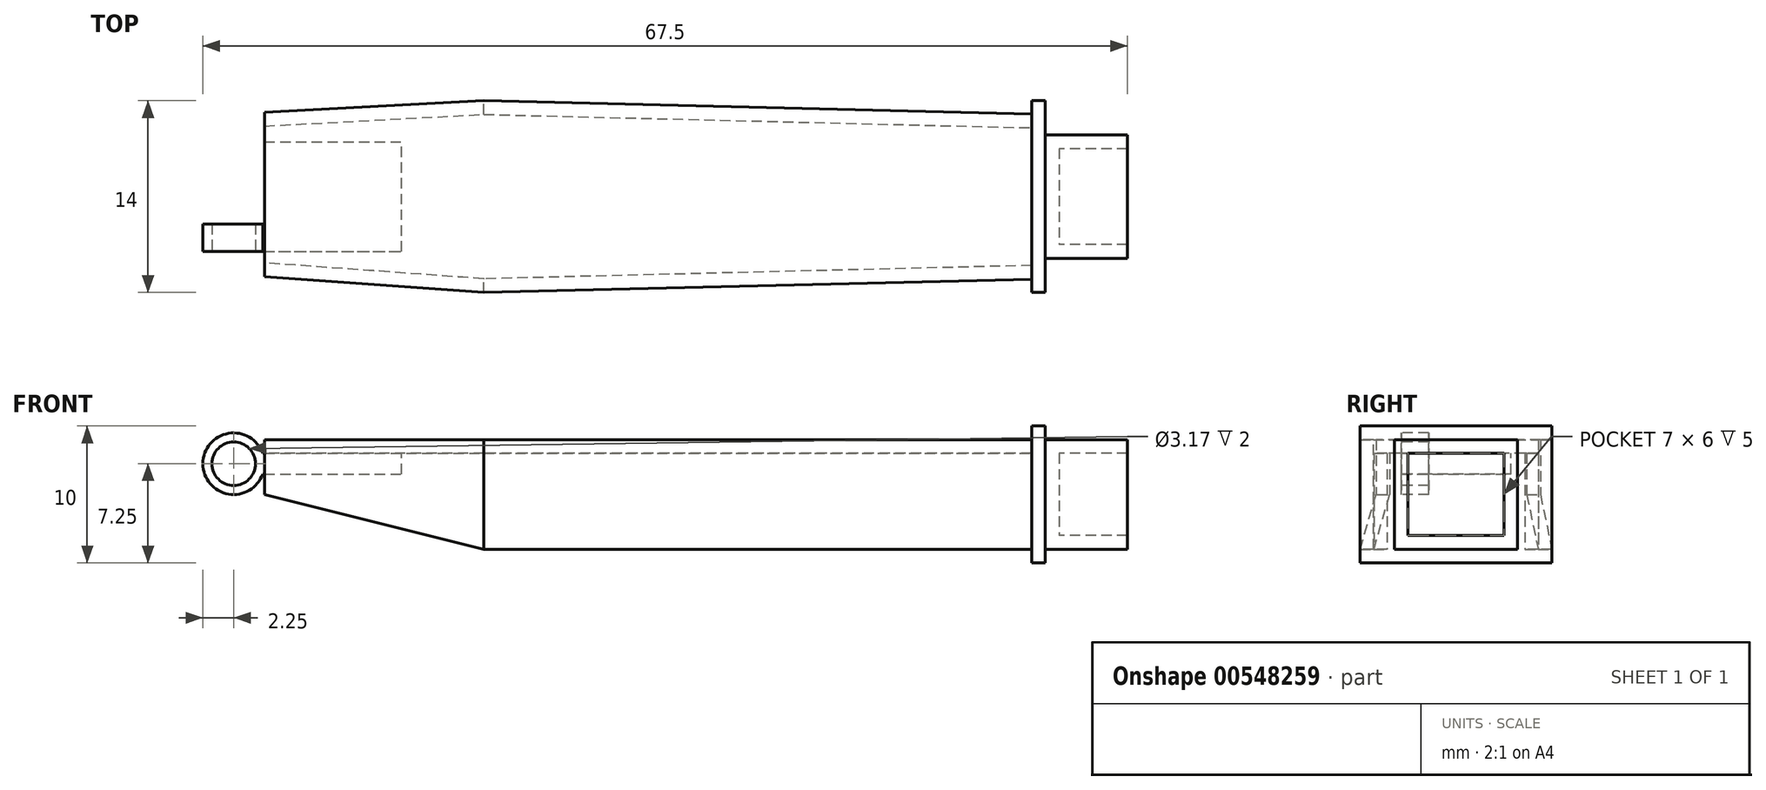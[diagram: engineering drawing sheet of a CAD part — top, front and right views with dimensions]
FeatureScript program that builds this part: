
annotation { "Feature Type Name" : "Feature", "Feature Type Description" : "" }
export const myFeature = defineFeature(function(context is Context, id is Id, definition is map)
    precondition{}
    {
        {
            var Q0;
            Q0=qCreatedBy(makeId("Top.planeOp"),FACE);
            var sketch = newSketch(context, id + "F0", { "sketchPlane" : qUnion([Q0])});
            skLineSegment(sketch, "E0", {"start": v(0, 6.16) * mm, "end": v(0, -5.84) * mm});
            skLineSegment(sketch, "E1", {"start": v(0, 6.16) * mm, "end": v(16, 7) * mm});
            skLineSegment(sketch, "E2", {"start": v(16, 7) * mm, "end": v(57, 6) * mm});
            skLineSegment(sketch, "E3", {"start": v(57, 6) * mm, "end": v(57, -6) * mm});
            skLineSegment(sketch, "E4", {"start": v(57, -6) * mm, "end": v(16, -7) * mm});
            skLineSegment(sketch, "E5", {"start": v(16, -7) * mm, "end": v(0, -5.84) * mm});
            skLineSegment(sketch, "E6", {"start": v(0, 0) * mm, "end": v(16, 0) * mm, "construction": true});
            skLineSegment(sketch, "E7", {"start": v(16, 7) * mm, "end": v(16, -7) * mm, "construction": true});
            skLineSegment(sketch, "E8", {"start": v(16, 0) * mm, "end": v(57, 0) * mm, "construction": true});
            skSolve(sketch);
        }
        {
            var Q0;
            Q0 = qSketchRegion(id + "F0", true);
            extrude(context, id + "F1", {"entities" : qUnion([Q0]), "depth" : 8 * mm, "offsetDistance" : 25 * mm});
        }
        {
            var Q0;
            Q0=makeQuery(id+"F1.opExtrude","CAP_FACE",FACE,{"disambiguationData":[OSD([sQuery(id+"F0.wireOp",EDGE,"E0"),sQuery(id+"F0.wireOp",EDGE,"E1"),sQuery(id+"F0.wireOp",EDGE,"E2"),sQuery(id+"F0.wireOp",EDGE,"E3"),sQuery(id+"F0.wireOp",EDGE,"E4"),sQuery(id+"F0.wireOp",EDGE,"E5")])],"isStart":true});
            var Q1;
            Q1=makeQuery(id+"F1.opExtrude","SWEPT_FACE",FACE,{"disambiguationData":[OSD([sQuery(id+"F0.wireOp",EDGE,"E0")])]});
            shell(context, id + "F2", {"entities" : qUnion([Q0, Q1]), "thickness" : 1 * mm});
        }
        {
            var Q0;
            Q0=qCreatedBy(makeId("Front.planeOp"),FACE);
            var sketch = newSketch(context, id + "F3", { "sketchPlane" : qUnion([Q0])});
            skLineSegment(sketch, "E9", {"start": v(0, 0) * mm, "end": v(0, 4) * mm});
            skLineSegment(sketch, "E10", {"start": v(0, 4) * mm, "end": v(16, 0) * mm});
            skLineSegment(sketch, "E11", {"start": v(16, 0) * mm, "end": v(0, 0) * mm});
            skLineSegment(sketch, "E12.0", {"start": v(57, 0) * mm, "end": v(16, 0) * mm, "construction": true});
            skSolve(sketch);
        }
        {
            var Q0;
            Q0 = qSketchRegion(id + "F3", true);
            extrude(context, id + "F4", {"entities" : qUnion([Q0]), "operationType" : NewBodyOperationType.REMOVE, "endBound" : BoundingType.SYMMETRIC, "depth" : 14.2 * mm, "offsetDistance" : 25 * mm});
        }
        {
            var Q0;
            Q0=makeQuery(id+"F1.opExtrude","SWEPT_FACE",FACE,{"disambiguationData":[OSD([sQuery(id+"F0.wireOp",EDGE,"E3")])]});
            var sketch = newSketch(context, id + "F5", { "sketchPlane" : qUnion([Q0])});
            skLineSegment(sketch, "E13.bottom", {"start": v(7, 9) * mm, "end": v(-7, 9) * mm});
            skLineSegment(sketch, "E13.top", {"start": v(7, -1) * mm, "end": v(-7, -1) * mm});
            skLineSegment(sketch, "E13.left", {"start": v(7, 9) * mm, "end": v(7, -1) * mm});
            skLineSegment(sketch, "E13.right", {"start": v(-7, 9) * mm, "end": v(-7, -1) * mm});
            skPoint(sketch, "E13.middle", {"position": v(0, 4) * mm});
            skPoint(sketch, "E13.middle.positionSnap0", {"position": v(6, 4) * mm});
            skPoint(sketch, "E13.centerSnap0", {"position": v(6, 4) * mm});
            skSolve(sketch);
        }
        {
            var Q0;
            Q0 = qSketchRegion(id + "F5", true);
            extrude(context, id + "F6", {"entities" : qUnion([Q0]), "operationType" : NewBodyOperationType.ADD, "oppositeDirection" : true, "depth" : 1 * mm, "offsetDistance" : 25 * mm});
        }
        {
            var Q0;
            Q0=makeQuery(id+"F6.boolean.opBoolean","MERGE",FACE,{"derivedFrom":[makeQuery(id+"F1.opExtrude","SWEPT_FACE",FACE,{"disambiguationData":[OSD([sQuery(id+"F0.wireOp",EDGE,"E3")])]}),makeQuery(id+"F6.opExtrude","CAP_FACE",FACE,{"disambiguationData":[OSD([sQuery(id+"F5.wireOp",EDGE,"E13.bottom"),sQuery(id+"F5.wireOp",EDGE,"E13.top"),sQuery(id+"F5.wireOp",EDGE,"E13.left"),sQuery(id+"F5.wireOp",EDGE,"E13.right")])],"isStart":true})]});
            var sketch = newSketch(context, id + "F7", { "sketchPlane" : qUnion([Q0])});
            skLineSegment(sketch, "E14.bottom", {"start": v(4.5, 8) * mm, "end": v(-4.5, 8) * mm});
            skLineSegment(sketch, "E14.top", {"start": v(4.5, 0) * mm, "end": v(-4.5, 0) * mm});
            skLineSegment(sketch, "E14.left", {"start": v(4.5, 8) * mm, "end": v(4.5, 0) * mm});
            skLineSegment(sketch, "E14.right", {"start": v(-4.5, 8) * mm, "end": v(-4.5, 0) * mm});
            skPoint(sketch, "E14.middle", {"position": v(0, 4) * mm});
            skPoint(sketch, "E14.middle.positionSnap0", {"position": v(-7, 4) * mm});
            skPoint(sketch, "E14.centerSnap0", {"position": v(-7, 4) * mm});
            skSolve(sketch);
        }
        {
            var Q0;
            Q0 = qSketchRegion(id + "F7", true);
            extrude(context, id + "F8", {"entities" : qUnion([Q0]), "depth" : 6 * mm, "offsetDistance" : 25 * mm});
        }
        {
            var Q0;
            Q0=makeQuery(id+"F8.opExtrude","CAP_FACE",FACE,{"disambiguationData":[OSD([sQuery(id+"F7.wireOp",EDGE,"E14.bottom"),sQuery(id+"F7.wireOp",EDGE,"E14.top"),sQuery(id+"F7.wireOp",EDGE,"E14.left"),sQuery(id+"F7.wireOp",EDGE,"E14.right")])],"isStart":false});
            shell(context, id + "F9", {"entities" : qUnion([Q0]), "thickness" : 1 * mm});
        }
        {
            var Q0;
            Q0=makeQuery(id+"F2.opShell","OFFSET_FACE",FACE,{"disambiguationData":[OSD([sQuery(id+"F0.wireOp",EDGE,"E0"),sQuery(id+"F0.wireOp",EDGE,"E1"),sQuery(id+"F0.wireOp",EDGE,"E2"),sQuery(id+"F0.wireOp",EDGE,"E3"),sQuery(id+"F0.wireOp",EDGE,"E4"),sQuery(id+"F0.wireOp",EDGE,"E5")])]});
            var sketch = newSketch(context, id + "F10", { "sketchPlane" : qUnion([Q0])});
            skLineSegment(sketch, "E15.bottom", {"start": v(0, 4) * mm, "end": v(10, 4) * mm});
            skLineSegment(sketch, "E15.top", {"start": v(0, -4) * mm, "end": v(10, -4) * mm});
            skLineSegment(sketch, "E15.left", {"start": v(0, 4) * mm, "end": v(0, -4) * mm});
            skLineSegment(sketch, "E15.right", {"start": v(10, 4) * mm, "end": v(10, -4) * mm});
            skLineSegment(sketch, "E16", {"start": v(-2.82, 0) * mm, "end": v(14.2, 0) * mm, "construction": true});
            skPoint(sketch, "E16.startSnap0", {"position": v(0, 0) * mm});
            skSolve(sketch);
        }
        {
            var Q0;
            Q0 = qSketchRegion(id + "F10", true);
            extrude(context, id + "F11", {"entities" : qUnion([Q0]), "operationType" : NewBodyOperationType.ADD, "depth" : 1.5 * mm, "offsetDistance" : 25 * mm});
        }
        {
            var Q0;
            Q0=makeQuery(id+"F11.opExtrude","SWEPT_FACE",FACE,{"disambiguationData":[OSD([sQuery(id+"F10.wireOp",EDGE,"E15.bottom")])]});
            var sketch = newSketch(context, id + "F12", { "sketchPlane" : qUnion([Q0])});
            skCircle(sketch, "E17", {"center": v(-2.25, 6.25) * mm, "radius": 2.25 * mm});
            skPoint(sketch, "E17.centerSnap0", {"position": v(0, 6.25) * mm});
            skCircle(sketch, "E18", {"center": v(-2.25, 6.25) * mm, "radius": 1.59 * mm});
            skLineSegment(sketch, "E19", {"start": v(0, 5.5) * mm, "end": v(-0.13, 5.5) * mm});
            skLineSegment(sketch, "E20", {"start": v(0, 7) * mm, "end": v(-0.13, 7) * mm});
            skSolve(sketch);
        }
        {
            var Q0;
            Q0 = qSketchRegion(id + "F12", true);
            var Q1;
            {var subQ0=sQuery(id+"F12.wireOp",EDGE,"E20");Q1=makeQuery(id+"F12.imprint","IMPRINT",FACE,{"disambiguationData":[TD([[makeQuery(id+"F12.imprint","IMPRINT",EDGE,{"derivedFrom":subQ0}),1.0]])]});}
            var Q2;
            {var subQ0=sQuery(id+"F12.wireOp",EDGE,"E19");Q2=makeQuery(id+"F12.imprint","IMPRINT",FACE,{"disambiguationData":[TD([[makeQuery(id+"F12.imprint","IMPRINT",EDGE,{"derivedFrom":subQ0}),-1.0]])]});}
            extrude(context, id + "F13", {"entities" : qUnion([Q0, Q1, Q2]), "operationType" : NewBodyOperationType.ADD, "oppositeDirection" : true, "depth" : 2 * mm, "offsetDistance" : 25 * mm});
        }
    });
